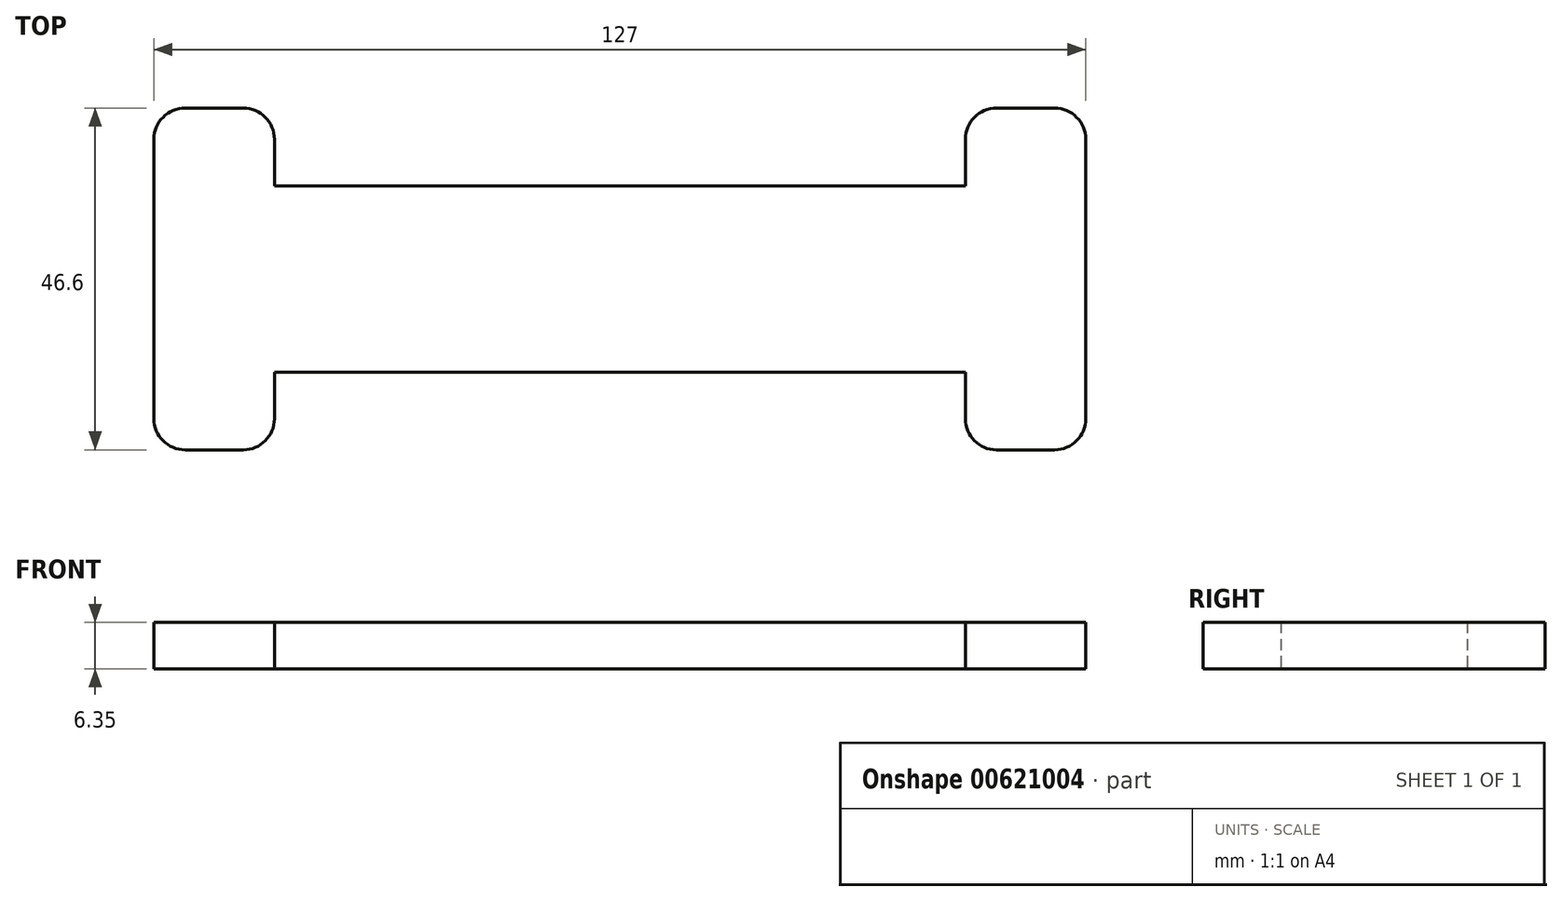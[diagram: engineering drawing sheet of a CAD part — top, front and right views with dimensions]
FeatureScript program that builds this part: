
annotation { "Feature Type Name" : "Feature", "Feature Type Description" : "" }
export const myFeature = defineFeature(function(context is Context, id is Id, definition is map)
    precondition{}
    {
        {
            var Q0;
            Q0=qCreatedBy(makeId("Top.planeOp"),FACE);
            var sketch = newSketch(context, id + "F0", { "sketchPlane" : qUnion([Q0])});
            skLineSegment(sketch, "E0.bottom", {"start": v(0, 0) * mm, "end": v(127, 0) * mm});
            skLineSegment(sketch, "E0.top", {"start": v(0, 25.4) * mm, "end": v(127, 25.4) * mm});
            skLineSegment(sketch, "E0.left", {"start": v(0, 0) * mm, "end": v(0, 25.4) * mm});
            skLineSegment(sketch, "E0.right", {"start": v(127, 0) * mm, "end": v(127, 25.4) * mm});
            skLineSegment(sketch, "E1", {"start": v(0, 0) * mm, "end": v(0, -6.35) * mm});
            skArc(sketch, "E2", {"start": v(0, -6.35) * mm, "mid": v(1.24, -9.35) * mm, "end": v(4.25, -10.6) * mm});
            skLineSegment(sketch, "E3", {"start": v(4.25, -10.6) * mm, "end": v(12.17, -10.6) * mm});
            skArc(sketch, "E4", {"start": v(12.17, -10.6) * mm, "mid": v(15.18, -9.35) * mm, "end": v(16.42, -6.35) * mm});
            skLineSegment(sketch, "E5", {"start": v(16.42, -6.35) * mm, "end": v(16.42, 0) * mm});
            skLineSegment(sketch, "E6", {"start": v(0, 25.4) * mm, "end": v(0, 31.75) * mm});
            skLineSegment(sketch, "E7", {"start": v(4.25, 36) * mm, "end": v(12.17, 36) * mm});
            skArc(sketch, "E8", {"start": v(0, 31.75) * mm, "mid": v(1.24, 34.75) * mm, "end": v(4.25, 36) * mm});
            skArc(sketch, "E9", {"start": v(12.17, 36) * mm, "mid": v(15.18, 34.75) * mm, "end": v(16.42, 31.75) * mm});
            skLineSegment(sketch, "E10", {"start": v(16.42, 31.75) * mm, "end": v(16.42, 25.4) * mm});
            skLineSegment(sketch, "E11", {"start": v(127, 25.4) * mm, "end": v(127, 31.75) * mm});
            skArc(sketch, "E12", {"start": v(127, 31.75) * mm, "mid": v(125.76, 34.75) * mm, "end": v(122.75, 36) * mm});
            skLineSegment(sketch, "E13", {"start": v(122.75, 36) * mm, "end": v(114.83, 36) * mm});
            skArc(sketch, "E14", {"start": v(114.83, 36) * mm, "mid": v(111.82, 34.75) * mm, "end": v(110.58, 31.75) * mm});
            skLineSegment(sketch, "E15", {"start": v(110.58, 31.75) * mm, "end": v(110.58, 25.4) * mm});
            skLineSegment(sketch, "E16", {"start": v(127, 0) * mm, "end": v(127, -6.35) * mm});
            skArc(sketch, "E17", {"start": v(127, -6.35) * mm, "mid": v(125.76, -9.35) * mm, "end": v(122.75, -10.6) * mm});
            skLineSegment(sketch, "E18", {"start": v(122.75, -10.6) * mm, "end": v(114.83, -10.6) * mm});
            skArc(sketch, "E19", {"start": v(114.83, -10.6) * mm, "mid": v(111.82, -9.35) * mm, "end": v(110.58, -6.35) * mm});
            skLineSegment(sketch, "E20", {"start": v(110.58, -6.35) * mm, "end": v(110.58, 0) * mm});
            skSolve(sketch);
        }
        {
            var Q0;
            Q0 = qSketchRegion(id + "F0", true);
            extrude(context, id + "F1", {"entities" : qUnion([Q0]), "depth" : 6.35 * mm, "offsetDistance" : 25.4 * mm});
        }
    });
